# Revit family: NBS_HeatraeSadia_IndrctHotWtrStrgCylndrsDblFeed_MEGAFLOEcoIndirect
name_source: partatom
category: Plumbing Fixtures
revit_build: Autodesk Revit 2014 (Build: 20130709_2115(x64)
units: mm (PartAtom-declared; Revit-internal decimal feet)

## types (1)
- NBS_HeatraeSadia_IndrctHotWtrStrgCylndrsDblFeed_MEGAFLOEcoIndirect
    Accessories = Swept tee for direct secondary return (94:970:033), Titanium indirect control assembly and immersion heater accessory pack (95:970:554)
    AssetType = Fixed
    BIMObjectName = NBS_HeatraeSadia_IndirectHotWaterStorageCylindersDoubleFeed_MEGAFLOEco-145i
    CW Connection = Yes
    Color = White
    Connections = Inlets and outlets: ¾" BSP male parallel and 22 mm compression fittings; Coil: ¾" BSP male parallel and 22 mm compression fittings; ½" temperature and pressure relief valve: 15 mm compression outlet
    ControlHousingMaterial = NBS_Concept
    CylinderMaterial = NBS_Concept
    Description = Unvented indirect hot water cylinders
    DurationUnit = year
    EffectiveCapacity = 0 m³
    ElectricalDeviceNominalPower = 18700
    ErPRating = B
    Features = Patented internal floating baffle system to accommodate water expansion, no anode, insulated casing for the temperature and pressure relief valve, unique 'L-shaped' long-life Superloy immersion heater reaches deeper into the tank giving more hot water, patented cold water inlet diffuser, high performance 'coil-in-coil' heat exchanger, exceeds CHeSS Best Practice for recovery times and insulation
    FirstCurvatureRadius = 0 mm  [stored 0 ft]
    Fixing = Floor fixed
    FlowRate = ≤72 L/min
    HW Connection = Yes
    HasProtectiveEarth = No
    HeatUpTime = 24 minutes
    Height = 1102 mm  [stored 3.61549 ft]
    IfcExportAs = IfcTankType
    IfcExportType = STORAGE
    ImmersionHeater = One long-life 3 kW Superloy 825 alloy sheathed element with integral thermostat and thermal cut-out
    ManufacturerName = Heatrae Sadia
    ManufacturerURL = www.heatraesadia.com
    Material = Outer casing: Plastic-coated corrosion-proofed steel; Water container: Duplex stainless steel with internal air-gap system
    MaterialThickness = 0 mm  [stored 0 ft]
    ModelNumber = 95:050:463
    ModelReference = MEGAFLO Eco - 145i
    NBSCertification = http://www.nationalbimlibrary.com
    NBSDescription = Indirect hot water storage cylinders, double feed
    NBSReference = 90-15-35/350
    Name = IndirectHotWaterStorageCylindersDoubleFeed_MEGAFLOEco-145i_HeatraeSadia
    NominalCapacity = 4.11 m³
    NominalCurrent = 0
    NominalDepth = 1102 mm  [stored 3.61549 ft]
    NominalFrequencyRange = 50.0, 60.0
    NominalLengthOrDiameter = 579 mm
    NominalVoltage = 230.0, 240.0
    NominalWidthOrDiameter = 579 mm
    NumberOfPoles = 0
    OperatingWeight = 35
    OutletTemperatureRange = 12-68°C
    PatternType = Vertical cylinder
    PhaseAngle = 0.00°
    PrimaryCoilSurfaceArea = 0.72 m²
    PrimaryCoilType = 22 mm diameter stainless steel
    ProductInformation = www.heatraesadia.com/docs/344-104_Megaflo_Eco_Tech_Sep_15.pdf
    RecoveryTime = 17 minutes
    SafetyFeatures = High limit thermal cut-out operates at 90°C, wired in series with two-port motorised valve, temperature and pressure relief valve factory set to operate at 10 bar and 90°C
    SecondCurvatureRadius = 0 mm  [stored 0 ft]
    SecondaryReturnAvailability = Secondary Return
    SecondaryReturnHeight = 709 mm  [stored 2.32612 ft]
    Shape = Cylinder
    Size = 1229 x 579 x 579 mm
    SupplyPressureRange = 1.5-16.0 bar
    TemperaturePressureReliefValveHeight = 794 mm
    ThermalInsulation = 60 mm thick CFC/HCFC free (ODP zero) polyurethane
    ThirdPartyCertification = Kiwa approved, Nemko approved
    Uniclass2 = 90-90-87/423
    Uniclass2015Description = Double feed indirect hot water storage cylinders
    Uniclass2015Reference = Pr_60_50_20_23
    Uniclass2015Version = Products v1.1
    UsageCurrent = 0
    ValveMaterial = NBS_Concept
    Vent Connection = Yes
    Version = 1
    WarrantyDurationParts = 2
    WarrantyDurationUnit = year
    WarrantyStartDate = 1900-12-31T23:59:59
    Waste Connection = No
    Width = 579 mm

note: [stored X ft] marks values corroborated as IEEE doubles in the binary element streams (Revit-internal decimal feet)

## geometry (parser evidence)
native form markers: Blend x3, Sweep x8
no freeform markers — native parametric forms only
